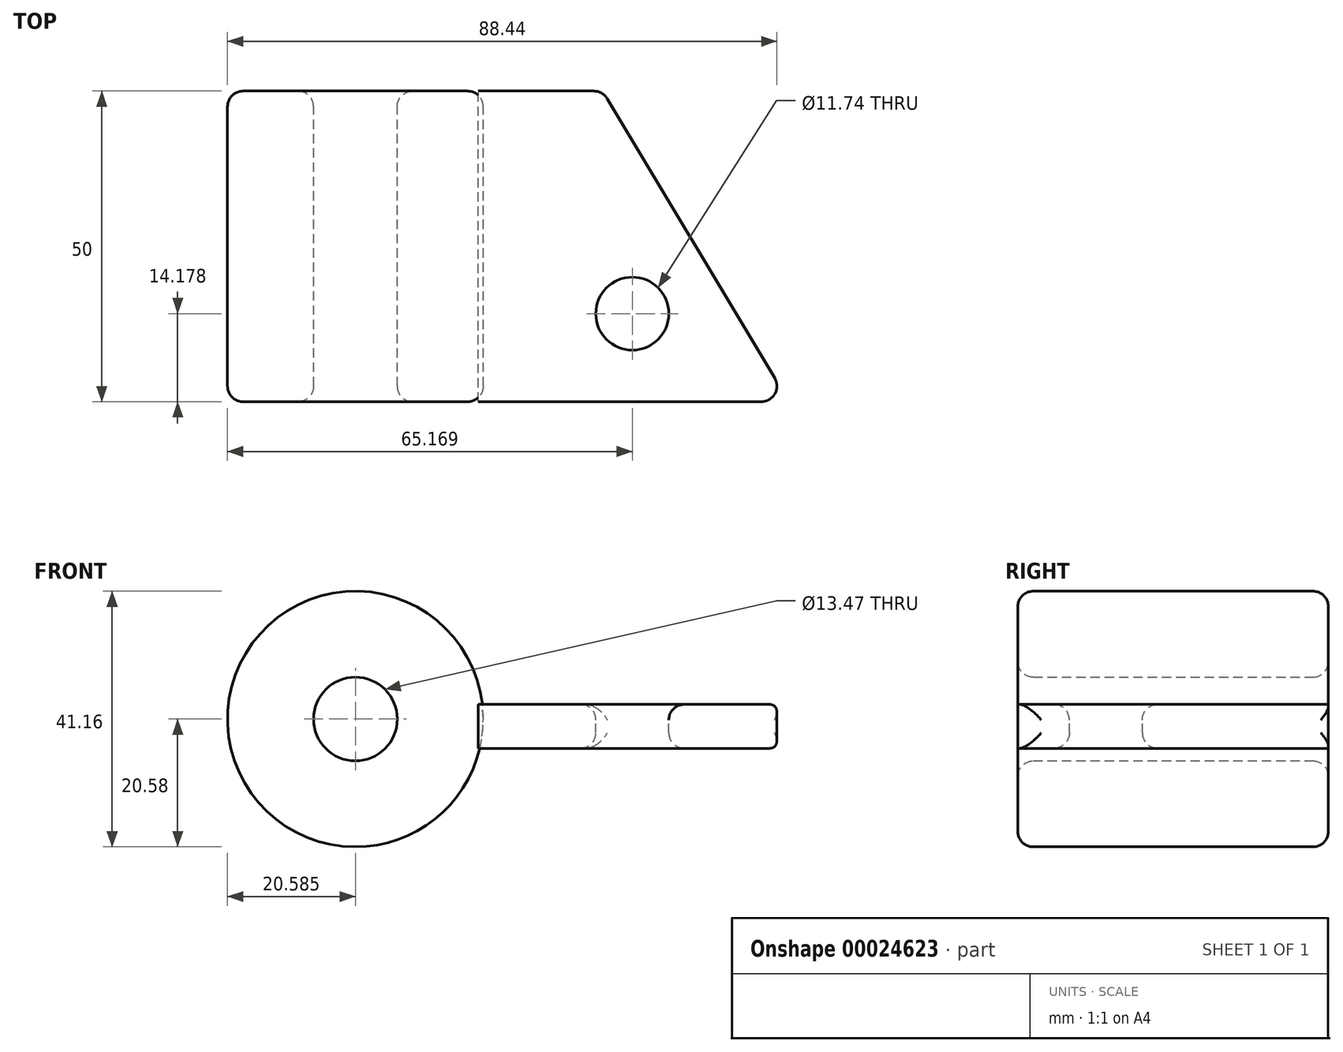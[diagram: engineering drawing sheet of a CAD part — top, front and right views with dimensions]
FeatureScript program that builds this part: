
annotation { "Feature Type Name" : "Feature", "Feature Type Description" : "" }
export const myFeature = defineFeature(function(context is Context, id is Id, definition is map)
    precondition{}
    {
        {
            var Q0;
            Q0=qCreatedBy(makeId("Front.planeOp"),FACE);
            var sketch = newSketch(context, id + "F0", { "sketchPlane" : qUnion([Q0])});
            skCircle(sketch, "E0", {"center": v(-44.76, 6.82) * mm, "radius": 20.58 * mm});
            skCircle(sketch, "E1", {"center": v(-44.76, 6.82) * mm, "radius": 6.74 * mm});
            skSolve(sketch);
        }
        {
            var Q0;
            Q0=makeQuery(id+"F0.imprint","IMPRINT",FACE,{"disambiguationData":[TD([[makeQuery(id+"F0.imprint","IMPRINT",EDGE,{"derivedFrom":sQuery(id+"F0.wireOp",EDGE,"E0")}),1.0]])]});
            extrude(context, id + "F1", {"entities" : qUnion([Q0]), "depth" : 50 * mm});
        }
        {
            var Q0;
            Q0=qCreatedBy(makeId("Right.planeOp"),FACE);
            var sketch = newSketch(context, id + "F2", { "sketchPlane" : qUnion([Q0])});
            skLineSegment(sketch, "E2.bottom", {"start": v(-50.14, 9.18) * mm, "end": v(0, 9.18) * mm});
            skLineSegment(sketch, "E2.top", {"start": v(-50.14, 2.1) * mm, "end": v(0, 2.1) * mm});
            skLineSegment(sketch, "E2.left", {"start": v(-50.14, 9.18) * mm, "end": v(-50.14, 2.1) * mm});
            skLineSegment(sketch, "E2.right", {"start": v(0, 9.18) * mm, "end": v(0, 2.1) * mm});
            skSolve(sketch);
        }
        {
            var Q0;
            Q0=makeQuery(id+"F2.imprint","IMPRINT",FACE,{"disambiguationData":[TD([[makeQuery(id+"F2.imprint","IMPRINT",EDGE,{"derivedFrom":sQuery(id+"F2.wireOp",EDGE,"E2.bottom")}),-1.0]])]});
            extrude(context, id + "F3", {"entities" : qUnion([Q0]), "oppositeDirection" : true, "depth" : 25 * mm});
        }
        {
            var Q0;
            Q0=makeQuery(id+"F3.opExtrude","CAP_FACE",FACE,{"disambiguationData":[OSD([sQuery(id+"F2.wireOp",EDGE,"E2.bottom"),sQuery(id+"F2.wireOp",EDGE,"E2.top"),sQuery(id+"F2.wireOp",EDGE,"E2.left"),sQuery(id+"F2.wireOp",EDGE,"E2.right")])],"isStart":true});
            extrude(context, id + "F4", {"entities" : qUnion([Q0]), "operationType" : NewBodyOperationType.ADD, "depth" : 25 * mm});
        }
        {
            var Q0;
            {var subQ0=sQuery(id+"F2.wireOp",EDGE,"E2.left");Q0=makeQuery(id+"F4.boolean.opBoolean","MERGE",FACE,{"derivedFrom":[makeQuery(id+"F3.opExtrude","SWEPT_FACE",FACE,{"disambiguationData":[OSD([subQ0])]}),makeQuery(id+"F4.opExtrude","SWEPT_FACE",FACE,{"disambiguationData":[OSD([subQ0])]})]});}
            var Q1;
            Q1=makeQuery(id+"F1.opExtrude","CAP_FACE",FACE,{"disambiguationData":[OSD([sQuery(id+"F0.wireOp",EDGE,"E0"),sQuery(id+"F0.wireOp",EDGE,"E1")])],"isStart":false});
            extrude(context, id + "F5", {"entities" : qUnion([Q0]), "operationType" : NewBodyOperationType.REMOVE, "endBound" : BoundingType.UP_TO_SURFACE, "oppositeDirection" : true, "endBoundEntityFace" : qUnion([Q1]), "depth" : 25 * mm});
        }
        {
            var Q0;
            {var subQ0=sQuery(id+"F2.wireOp",EDGE,"E2.bottom");Q0=makeQuery(id+"F4.boolean.opBoolean","MERGE",FACE,{"derivedFrom":[makeQuery(id+"F3.opExtrude","SWEPT_FACE",FACE,{"disambiguationData":[OSD([subQ0])]}),makeQuery(id+"F4.opExtrude","SWEPT_FACE",FACE,{"disambiguationData":[OSD([subQ0])]})]});}
            var sketch = newSketch(context, id + "F6", { "sketchPlane" : qUnion([Q0])});
            skLineSegment(sketch, "E3", {"start": v(25, -50) * mm, "end": v(-4.96, 0) * mm});
            skSolve(sketch);
        }
        {
            var Q0;
            {var subQ3=sQuery(id+"F6.wireOp",EDGE,"E3");Q0=makeQuery(id+"F6.imprint","IMPRINT",FACE,{"disambiguationData":[TD([[makeQuery(id+"F6.imprint","IMPRINT",EDGE,{"derivedFrom":subQ3}),-1.0]])]});}
            extrude(context, id + "F7", {"entities" : qUnion([Q0]), "operationType" : NewBodyOperationType.REMOVE, "endBound" : BoundingType.THROUGH_ALL, "oppositeDirection" : true, "depth" : 25 * mm});
        }
        {
            var Q0;
            {var subQ0=sQuery(id+"F2.wireOp",EDGE,"E2.bottom");Q0=makeQuery(id+"F4.boolean.opBoolean","MERGE",FACE,{"derivedFrom":[makeQuery(id+"F3.opExtrude","SWEPT_FACE",FACE,{"disambiguationData":[OSD([subQ0])]}),makeQuery(id+"F4.opExtrude","SWEPT_FACE",FACE,{"disambiguationData":[OSD([subQ0])]})]});}
            var sketch = newSketch(context, id + "F8", { "sketchPlane" : qUnion([Q0])});
            skCircle(sketch, "E4", {"center": v(-0.18, -35.82) * mm, "radius": 5.87 * mm});
            skSolve(sketch);
        }
        {
            var Q0;
            Q0=makeQuery(id+"F8.imprint","IMPRINT",FACE,{"disambiguationData":[TD([[makeQuery(id+"F8.imprint","IMPRINT",EDGE,{"derivedFrom":sQuery(id+"F8.wireOp",EDGE,"E4")}),1.0]])]});
            extrude(context, id + "F9", {"entities" : qUnion([Q0]), "operationType" : NewBodyOperationType.REMOVE, "endBound" : BoundingType.THROUGH_ALL, "oppositeDirection" : true, "depth" : 25 * mm});
        }
        {
            var Q0;
            Q0=makeQuery(id+"F1.opExtrude","SWEPT_FACE",FACE,{"disambiguationData":[OSD([sQuery(id+"F0.wireOp",EDGE,"E0")])]});
            var Q1;
            Q1=makeQuery(id+"F1.opExtrude","SWEPT_FACE",FACE,{"disambiguationData":[OSD([sQuery(id+"F0.wireOp",EDGE,"E1")])]});
            var Q2;
            Q2=makeQuery(id+"F9.boolean.opBoolean","COPY",FACE,{"derivedFrom":makeQuery(id+"F9.opExtrude","SWEPT_FACE",FACE,{"disambiguationData":[OSD([sQuery(id+"F8.wireOp",EDGE,"E4")])]})});
            var Q3;
            Q3=makeQuery(id+"F7.boolean.opBoolean","COPY",FACE,{"derivedFrom":makeQuery(id+"F7.opExtrude","SWEPT_FACE",FACE,{"disambiguationData":[OSD([sQuery(id+"F6.wireOp",EDGE,"E3")])]})});
            fillet(context, id + "F10", {"entities" : qUnion([Q0, Q1, Q2, Q3]), "radius" : 2.5 * mm, "tangentPropagation" : true, "allowEdgeOverflow" : false});
        }
    });
